# Revit family: 613271711_Mueble Aluvia Miel Elevado 40x35
name_source: partatom
category: Generic Models
units: mm (PartAtom-declared; Revit-internal decimal feet)

## family parameters
Always vertical = Yes
Can host rebar = No
Cut with Voids When Loaded = No
Host = Wall
OmniClass Number = 23.31.13.11
OmniClass Title = Single Sinks
Part Type = Normal
Room Calculation Point = No
Round Connector Dimension = Use Diameter
Shared = No

## types (1)
- Ref. 613271711 Mueble Aluvia Miel Con Lavamanos.
    Alto = 850 mm  [stored 2.78871 ft]
    Ancho = 396 mm
    Canto = PVC rígido 2 mm de calibre.
PVC Flexible 0,5 mm de calibre.
    Carga Máxima = 88,2 lb (40 kg).
    Creado por = IDD
    Densidad = 15mm 670 kg./m^3.
    Description = La línea ALUVIA viene a entregar de manera asequible una solución perfecta que combina
diseño y funcionalidad, ALUVIA se inspira en el movimiento y caída del agua en la
naturaleza, es por ello de sus formas orgánicas donde podemos obtener un producto
compacto y de líneas fluidas, que se adapta en espacios pequeños.
El principal beneficio de los muebles de esta línea es ser un producto compacto que brinda
al consumidor máxima capacidad de almacenamiento e ideal para espacios pequeños.
· Mueble compacto para espacios pequeños.
· Lavamanos 100% en porcelana.
· Grán capacidad de almacenamiento.
· Resistentes a la Humedad.
    Dimensiones Generales (H*W*P) = 21,8” x 15,59” x 13,58” (555 x 396 x 345 mm).
    Fecha de creación = 17/07/2020
    Garantía Herrajes = 1 año
    Garantía madera = 1 año
    Manufacturer = Corona
    Material = Corona_Madera_Aglomerada_Miel
    Material piezas interiores = Corona_Madera_Aglomerada_Plomo
    Peso Bruto aprox = 18,5 lb (8,4 kg).
    Peso Neto aprox = 17,2 lb (7,8 kg).
    Profundidad = 345 mm  [stored 1.13189 ft]
    Resistencia a la humedad = 8%.
    Resistencia al rayado = 700 ciclos.
    Textura = Habano: Poro - Gris: Soft.
    Tiempo de Armado = 60 Minutos
    URL = https://corona.co

note: [stored X ft] marks values corroborated as IEEE doubles in the binary element streams (Revit-internal decimal feet)

## geometry (parser evidence)
native form markers: Sweep x14
no freeform markers — native parametric forms only
